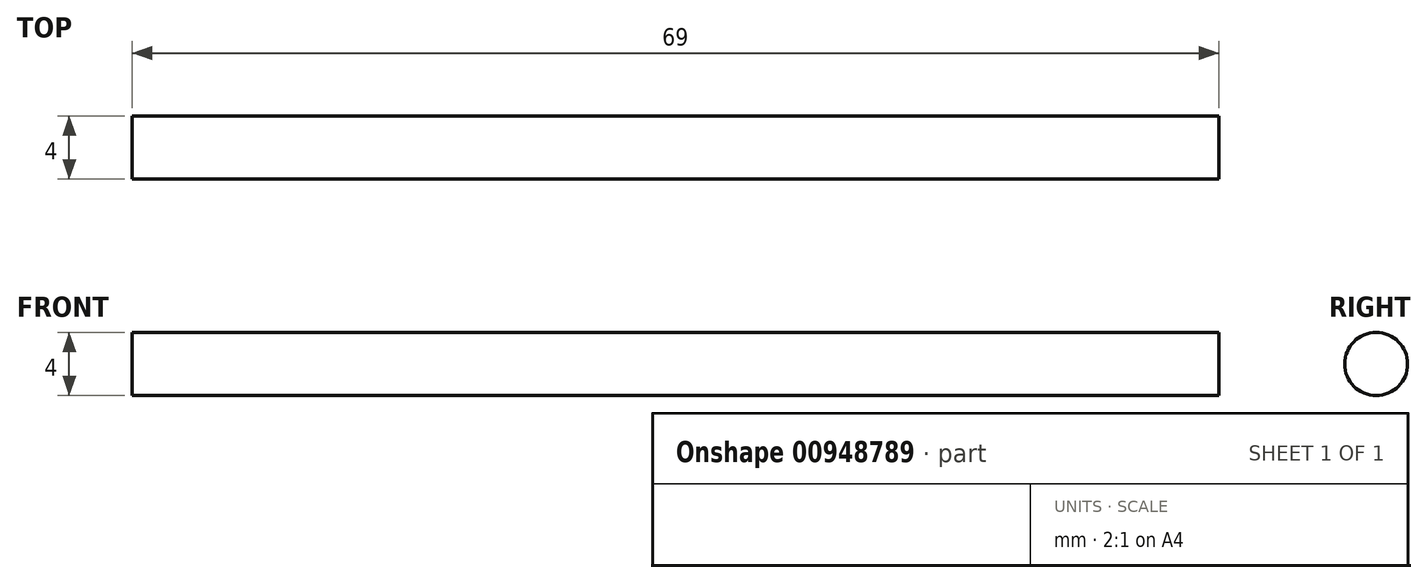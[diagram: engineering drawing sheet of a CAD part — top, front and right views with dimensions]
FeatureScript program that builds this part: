
annotation { "Feature Type Name" : "Feature", "Feature Type Description" : "" }
export const myFeature = defineFeature(function(context is Context, id is Id, definition is map)
    precondition{}
    {
        {
            var Q0;
            Q0=qCreatedBy(makeId("Right.planeOp"),FACE);
            var sketch = newSketch(context, id + "F0", { "sketchPlane" : qUnion([Q0])});
            skCircle(sketch, "E0", {"center": v(0, 0) * mm, "radius": 2 * mm});
            skSolve(sketch);
        }
        {
            var Q0;
            Q0 = qSketchRegion(id + "F0", true);
            extrude(context, id + "F1", {"entities" : qUnion([Q0]), "depth" : (57 + 12) * mm, "offsetDistance" : 25 * mm});
        }
    });
